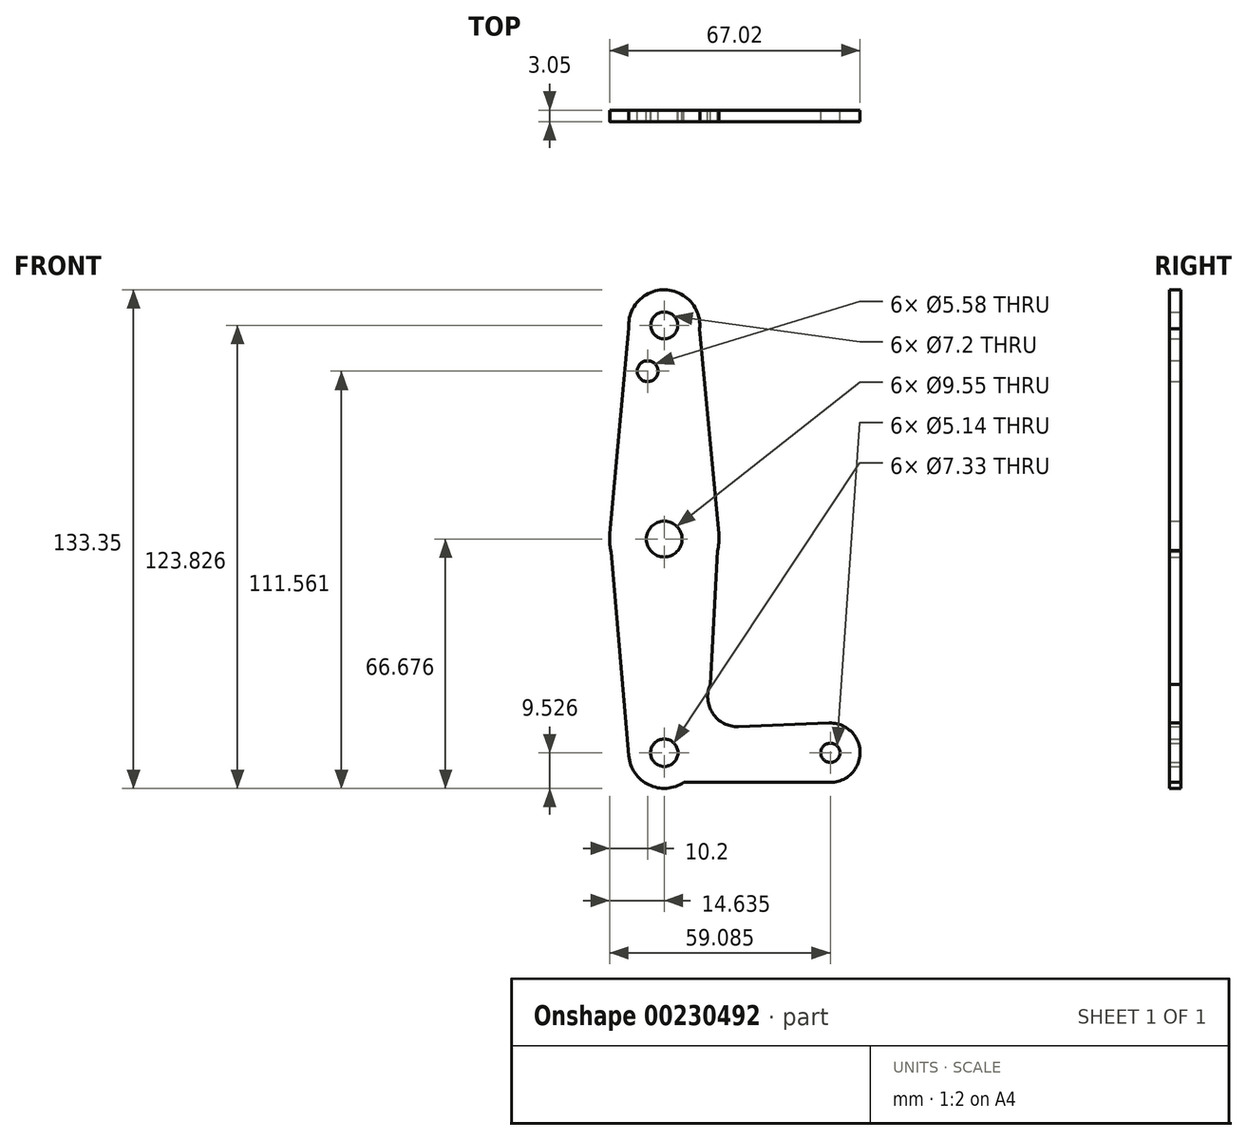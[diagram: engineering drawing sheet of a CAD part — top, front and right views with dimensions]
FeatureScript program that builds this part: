
annotation { "Feature Type Name" : "Feature", "Feature Type Description" : "" }
export const myFeature = defineFeature(function(context is Context, id is Id, definition is map)
    precondition{}
    {
        {
            var Q0;
            Q0=qCreatedBy(makeId("Front.planeOp"),FACE);
            var sketch = newSketch(context, id + "F0", { "sketchPlane" : qUnion([Q0])});
            skLineSegment(sketch, "E0", {"start": v(-45.8, 66.09) * mm, "end": v(-45.8, -48.21) * mm, "construction": true});
            skPoint(sketch, "E1.start.orphan", {"position": v(-45.8, -50.53) * mm});
            skLineSegment(sketch, "E2", {"start": v(-45.8, -48.21) * mm, "end": v(-29.93, -48.21) * mm, "construction": true});
            skCircle(sketch, "E3", {"center": v(-45.8, 66.09) * mm, "radius": 9.53 * mm});
            skCircle(sketch, "E4", {"center": v(-1.35, -48.21) * mm, "radius": 7.94 * mm});
            skCircle(sketch, "E5", {"center": v(-45.8, -48.21) * mm, "radius": 9.53 * mm});
            skLineSegment(sketch, "E6", {"start": v(-36.66, 68.75) * mm, "end": v(-36.43, 64.41) * mm});
            skLineSegment(sketch, "E7", {"start": v(-40.37, -44.78) * mm, "end": v(-41.98, -48.21) * mm});
            skLineSegment(sketch, "E8", {"start": v(-55.02, 68.49) * mm, "end": v(-55.24, 64.79) * mm});
            skLineSegment(sketch, "E9", {"start": v(-25.92, -41.22) * mm, "end": v(-1.66, -40.28) * mm});
            skLineSegment(sketch, "E10", {"start": v(-51.05, -56.16) * mm, "end": v(0, -56.15) * mm});
            skCircle(sketch, "E11", {"center": v(-45.8, -48.21) * mm, "radius": 3.67 * mm});
            skCircle(sketch, "E12", {"center": v(-1.35, -48.21) * mm, "radius": 2.57 * mm});
            skArc(sketch, "E13.filletArc", {"start": v(-33.43, -29.9) * mm, "mid": v(-32.85, -37.67) * mm, "end": v(-25.92, -41.22) * mm});
            skCircle(sketch, "E14", {"center": v(-50.24, 53.82) * mm, "radius": 2.8 * mm});
            skCircle(sketch, "E15", {"center": v(-45.8, 66.09) * mm, "radius": 3.6 * mm});
            skCircle(sketch, "E16", {"center": v(-45.8, 8.94) * mm, "radius": 14.64 * mm});
            skCircle(sketch, "E17", {"center": v(-45.8, 8.94) * mm, "radius": 4.78 * mm});
            skLineSegment(sketch, "E18", {"start": v(-36.66, 68.75) * mm, "end": v(-31.23, 10.29) * mm});
            skLineSegment(sketch, "E19", {"start": v(-55.02, 68.49) * mm, "end": v(-60.38, 10.28) * mm});
            skLineSegment(sketch, "E20.trimOffspring", {"start": v(-41.98, -48.21) * mm, "end": v(-1.35, -48.21) * mm, "construction": true});
            skLineSegment(sketch, "E21", {"start": v(-60.04, 5.56) * mm, "end": v(-55.3, -49.04) * mm});
            skLineSegment(sketch, "E22", {"start": v(-31.5, 5.81) * mm, "end": v(-33.43, -29.9) * mm});
            skPoint(sketch, "E23.start.orphan", {"position": v(-32.85, -37.67) * mm});
            skSolve(sketch);
        }
        {
            var Q0;
            Q0 = qSketchRegion(id + "F0", true);
            extrude(context, id + "F1", {"entities" : qUnion([Q0]), "depth" : 3.05 * mm});
        }
    });
